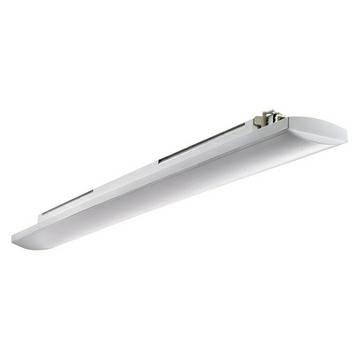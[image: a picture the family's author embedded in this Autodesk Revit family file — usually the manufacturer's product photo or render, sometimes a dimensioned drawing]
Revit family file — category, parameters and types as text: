
# Revit family: Lighting-Industriale-GEWISS-SMART[3]-PLAFONIERA-LED_OPALE_1600mm
name_source: partatom
category: Apparecchi per illuminazione
units: mm (PartAtom-declared; Revit-internal decimal feet)

## family parameters
Condiviso = No
Host = Superficie
Numero OmniClass = 23.80.70.11
Punto di calcolo locali = Sì
Quota connettore circolare = Usa diametro
Sorgente d'illuminazione = No
Taglio con vuoti quando caricato = No
Tipo di parte = Normale
Titolo OmniClass = Luminaries for Internal Lighting

## types (1)
- Lighting-Industriale-GEWISS-SMART[3]-PLAFONIERA-LED_OPALE_1600mm
    Apparecchio a ridotta temperatura superficiale = Conforme
    Applicazione = Interno
    Carico apparente = 55 VA
    Catalogo = LIGHTING
    Catalogo Serie = SMART [3]
    Classe di efficienza LED integrati = A ÷ A++
    Classe isolamento = II
    Codice EAN = 8011564877207
    Codice Electrocod = 2434
    Commenti sul wattaggio = 55W
    Descrizione = SMART3 1600 84LED 55W OPALE CABLAGGIO PASSANTE DALI 5700K
    Failure rate apparecchio (35.000h, Tq=35° C) = <2,5%
    Failure rate apparecchio (50.000h, Tq=25° C) = <2,5%
    Flusso nominale (lm) = 6900
    Ganci = GEWISS  - ALLUMINIO
    Garanzia = 5 anni
    Glow Wire Test = 850°C
    Grado di protezione = IP66/IP69
    IDF = 429fcb6a-c397-41af-9d66-92bec2f0642a
    IDT = e711e676-0d2c-4269-98d7-1f22e4a173c5
    Immagine tipo = GWS3158P.jpg
    LED Life time (L70) = 80000H
    LED Life time (L80B50) = 100000H
    LED Life time (L90B50) = 50000H
    LED LifeTime (L80B20) = 85000H
    Lampada = LED
    Lampada: = LED
    Lumen output (lm) = 6000
    Lunghezza = 1600 mm
    Lunghezza Lampada = 1600 mm  [stored 5.24934 ft]
    Modello = GWS3258PLD57K
    N° LED (#) = 84
    Peso (kg): = 2,5
    Potenza di sistema = 50W
    Produttore = GEWISS S.p.A.
    Prospetto di default = 1219 mm
    Resistenza agli urti = IK08
    SEO = Plafoniera
    Scheda Tecnica = https://www.gewiss.com
    Schermo = Opale con cablaggio passante
    Schermo. = Gewiss - Led Acceso
    Stampa 1_100 = Sì
    Stampa 1_200 = No
    Struttura = GEWISS - SMART 3 - GRIGIO
    Temperatura di colore = 5700 K (CRI 80)
    Temperatura di colore: = 5700 K (CRI 80)
    Temperatura di funzionamento = -25 +50 °C
    Temperatura di utilizzo = -30 +50 °C
    Tensione = 220/240 V - 50/60 Hz - Dali
    Tipo alimentatore = Driver Led in corrente continua
    Tipologia = DALI
    Tipologia sorgente luminosa = LED - Non sostituibile
    URL = https://www.gewiss.com
    Versione file RFA = 20.11

note: [stored X ft] marks values corroborated as IEEE doubles in the binary element streams (Revit-internal decimal feet)
